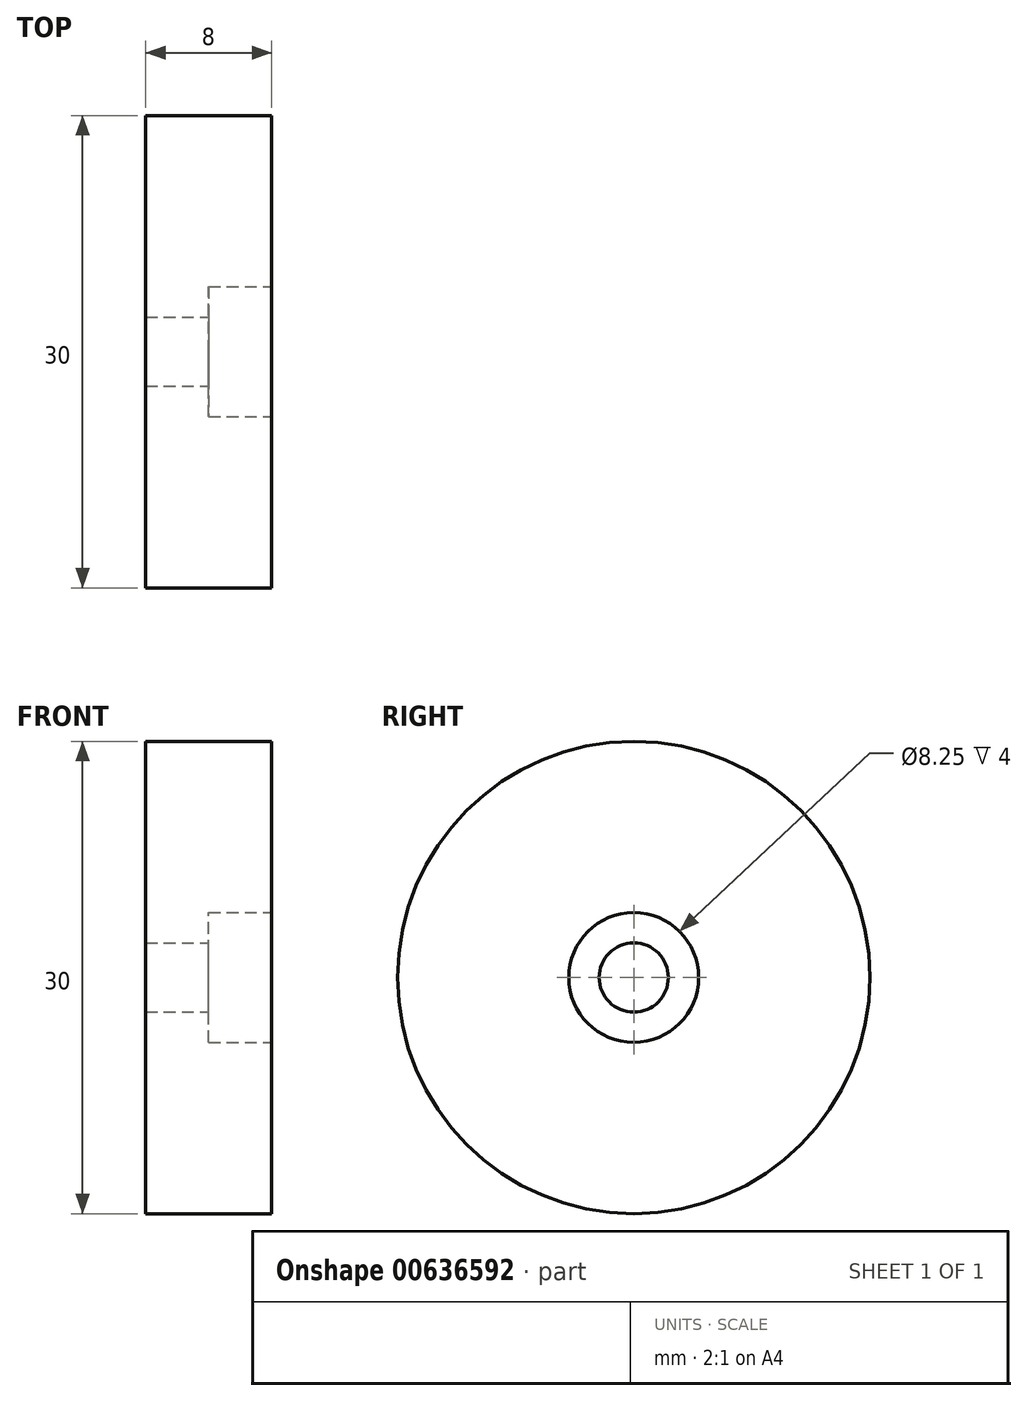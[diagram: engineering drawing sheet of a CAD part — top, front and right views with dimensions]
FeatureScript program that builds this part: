
annotation { "Feature Type Name" : "Feature", "Feature Type Description" : "" }
export const myFeature = defineFeature(function(context is Context, id is Id, definition is map)
    precondition{}
    {
        {
            var Q0;
            Q0=qCreatedBy(makeId("Right.planeOp"),FACE);
            var sketch = newSketch(context, id + "F0", { "sketchPlane" : qUnion([Q0])});
            skCircle(sketch, "E0", {"center": v(0, 0) * mm, "radius": 15 * mm});
            skSolve(sketch);
        }
        {
            var Q0;
            Q0 = qSketchRegion(id + "F0", true);
            extrude(context, id + "F1", {"entities" : qUnion([Q0]), "depth" : 8 * mm, "offsetDistance" : 25 * mm});
        }
        {
            var Q0;
            Q0=makeQuery(id+"F1.opExtrude","CAP_FACE",FACE,{"disambiguationData":[OSD([sQuery(id+"F0.wireOp",EDGE,"E0")])],"isStart":false});
            var sketch = newSketch(context, id + "F2", { "sketchPlane" : qUnion([Q0])});
            skPoint(sketch, "E1", {"position": v(0, 0) * mm});
            skSolve(sketch);
        }
        {
            var Q0;
            Q0=sQuery(id+"F2.wireOp",VERTEX,"E1");
            var Q1;
            Q1=makeQuery(id+"F1.opExtrude","SWEPT_BODY",BODY,{"disambiguationData":[OSD([sQuery(id+"F0.wireOp",EDGE,"E0")])]});
            hole(context, id + "F3", {"style" : HoleStyle.C_BORE, "endStyle" : HoleEndStyle.THROUGH, "standardTappedOrClearance" : lookupTablePath({ "standard" : "ISO", "fit" : "Normal", "size" : "M4", "type" : "Clearance" }), "standardBlindInLast" : lookupTablePath({ "fit" : "Standard", "standard" : "ISO", "size" : "M4", "type" : "Clearance" }), "holeDiameter" : 4.4 * mm, "cBoreDiameter" : 8.25 * mm, "cBoreDepth" : 4 * mm, "majorDiameter" : 5 * mm, "isTappedThrough" : true, "tappedDepth" : 5 * mm, "tapClearance" : 3, "locations" : qUnion([Q0]), "scope" : qUnion([Q1])});
        }
    });
